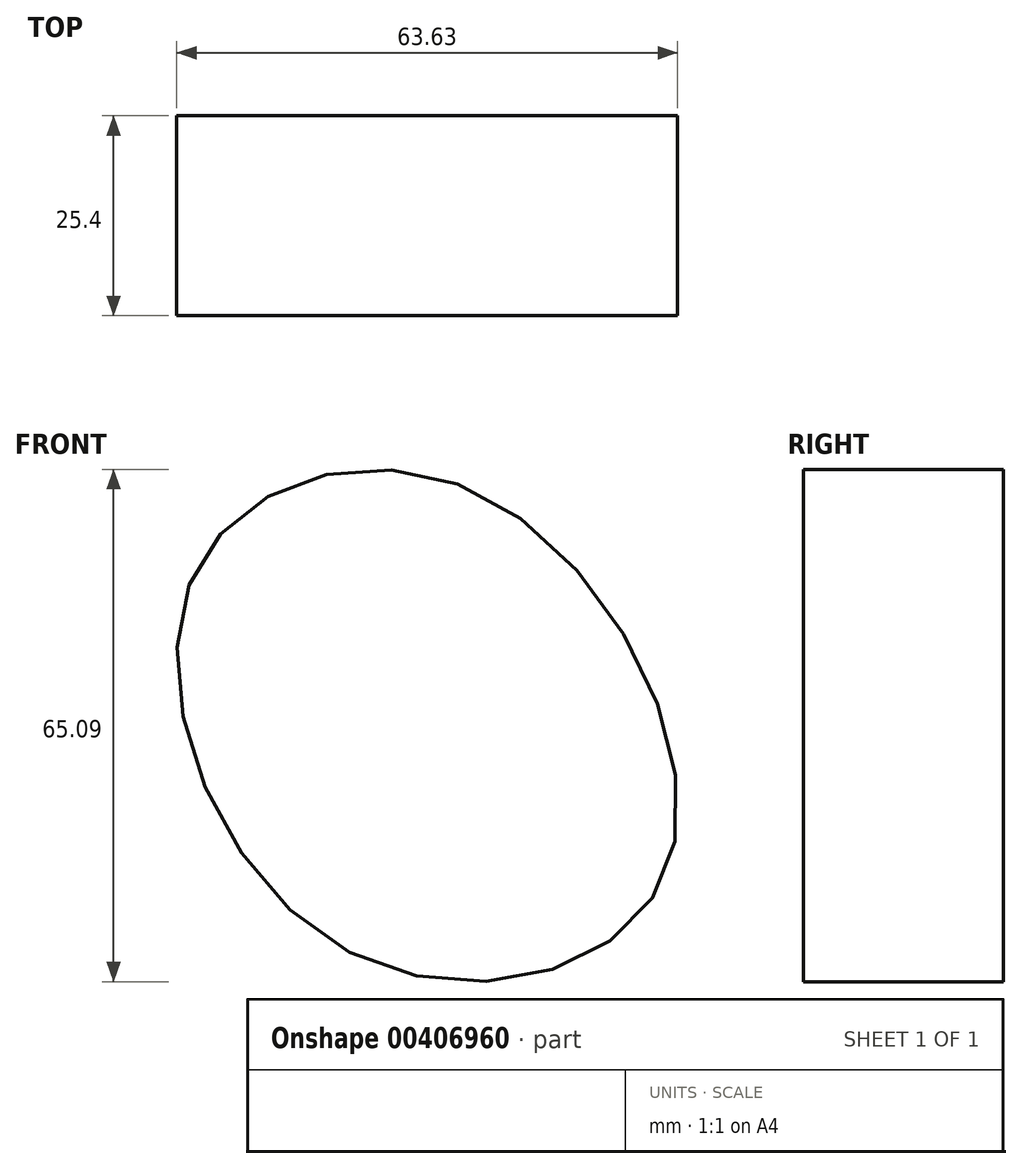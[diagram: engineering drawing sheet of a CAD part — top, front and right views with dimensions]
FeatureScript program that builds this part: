
annotation { "Feature Type Name" : "Feature", "Feature Type Description" : "" }
export const myFeature = defineFeature(function(context is Context, id is Id, definition is map)
    precondition{}
    {
        {
            var Q0;
            Q0=qCreatedBy(makeId("Front.planeOp"),FACE);
            var sketch = newSketch(context, id + "F0", { "sketchPlane" : qUnion([Q0])});
            skFitSpline(sketch, "E0", {"points": [v(-40.14, -9.95) * mm, v(0, 0) * mm, v(-23.82, 48.44) * mm, v(-60.28, 37.26) * mm, v(-40.14, -9.95) * mm]});
            skSolve(sketch);
        }
        {
            var Q0;
            Q0=makeQuery(id+"F0.imprint","IMPRINT",FACE,{"disambiguationData":[TD([[makeQuery(id+"F0.imprint","IMPRINT",EDGE,{"derivedFrom":sQuery(id+"F0.wireOp",EDGE,"E0")}),1.0]])]});
            extrude(context, id + "F1", {"entities" : qUnion([Q0]), "depth" : 25.4 * mm});
        }
    });
